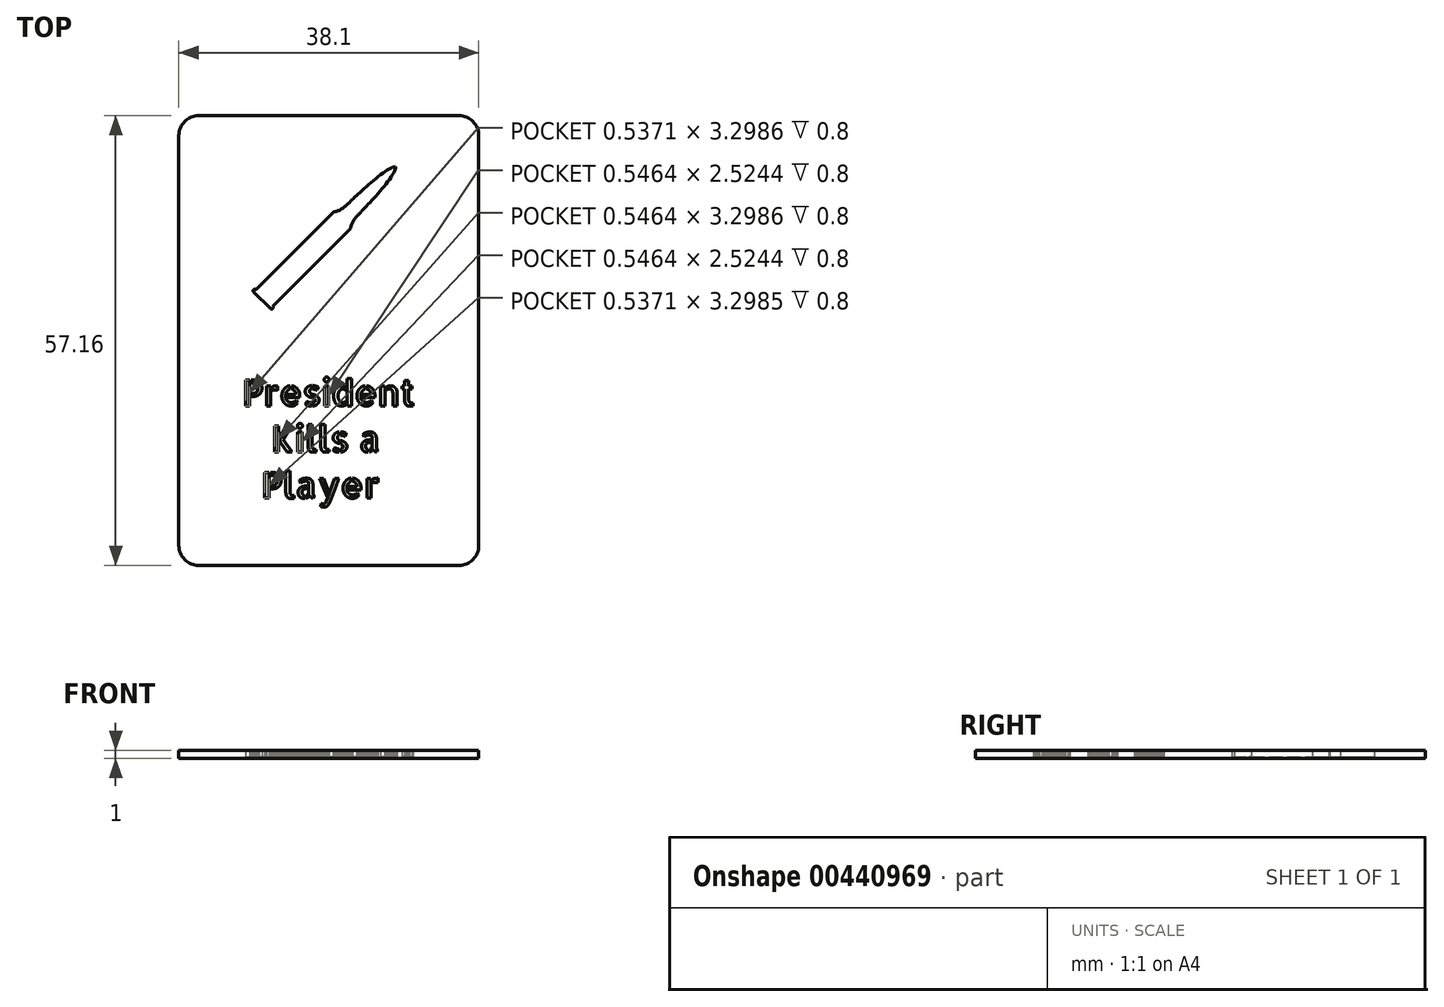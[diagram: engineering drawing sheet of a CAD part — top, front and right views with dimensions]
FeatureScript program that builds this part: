
annotation { "Feature Type Name" : "Feature", "Feature Type Description" : "" }
export const myFeature = defineFeature(function(context is Context, id is Id, definition is map)
    precondition{}
    {
        {
            var Q0;
            Q0=qCreatedBy(makeId("Top.planeOp"),FACE);
            var sketch = newSketch(context, id + "F0", { "sketchPlane" : qUnion([Q0])});
            skLineSegment(sketch, "E0.bottom", {"start": v(16.5, 28.58) * mm, "end": v(-16.51, 28.58) * mm});
            skLineSegment(sketch, "E0.top", {"start": v(16.51, -28.58) * mm, "end": v(-16.5, -28.58) * mm});
            skLineSegment(sketch, "E0.left", {"start": v(19.05, 26.04) * mm, "end": v(19.05, -26.04) * mm});
            skLineSegment(sketch, "E0.right", {"start": v(-19.05, 26.04) * mm, "end": v(-19.05, -26.04) * mm});
            skPoint(sketch, "E1.visualSharp", {"position": v(-19.05, 28.58) * mm});
            skArc(sketch, "E1.filletArc", {"start": v(-16.51, 28.58) * mm, "mid": v(-18.3, 27.83) * mm, "end": v(-19.05, 26.04) * mm});
            skPoint(sketch, "E2.visualSharp", {"position": v(19.05, 28.58) * mm});
            skArc(sketch, "E2.filletArc", {"start": v(19.05, 26.04) * mm, "mid": v(18.3, 27.83) * mm, "end": v(16.5, 28.58) * mm});
            skPoint(sketch, "E3.visualSharp", {"position": v(19.05, -28.58) * mm});
            skArc(sketch, "E3.filletArc", {"start": v(16.51, -28.58) * mm, "mid": v(18.3, -27.83) * mm, "end": v(19.05, -26.04) * mm});
            skPoint(sketch, "E4.visualSharp", {"position": v(-19.05, -28.58) * mm});
            skArc(sketch, "E4.filletArc", {"start": v(-19.05, -26.04) * mm, "mid": v(-18.3, -27.83) * mm, "end": v(-16.5, -28.58) * mm});
            skLineSegment(sketch, "E5", {"start": v(0, 28.58) * mm, "end": v(0, 0) * mm, "construction": true});
            skLineSegment(sketch, "E6", {"start": v(0, 0) * mm, "end": v(0, -28.58) * mm, "construction": true});
            skLineSegment(sketch, "E7", {"start": v(-8.49, 5.1) * mm, "end": v(-7.42, 4.05) * mm});
            skArc(sketch, "E8", {"start": v(-7.42, 4.05) * mm, "mid": v(-7.14, 4.05) * mm, "end": v(-7.14, 4.33) * mm});
            skLineSegment(sketch, "E9", {"start": v(-8.49, 5.1) * mm, "end": v(8.49, 22.08) * mm, "construction": true});
            skLineSegment(sketch, "E10", {"start": v(-7.14, 4.33) * mm, "end": v(2.76, 14.23) * mm});
            skFitSpline(sketch, "E11", {"points": [v(2.76, 14.23) * mm, v(4.17, 16.43) * mm], "startDerivative": vector(0.24, 3.05) * mm, "endDerivative": vector(0.39, 0.48) * mm});
            skFitSpline(sketch, "E12", {"points": [v(4.17, 16.43) * mm, v(8.49, 22.08) * mm], "startDerivative": vector(2.3, 2.45) * mm, "endDerivative": vector(-0.08, 3.52) * mm});
            skFitSpline(sketch, "E13.MirrorCS", {"points": [v(2.84, 17.77) * mm, v(8.49, 22.08) * mm], "startDerivative": vector(2.45, 2.3) * mm, "endDerivative": vector(3.52, -0.08) * mm});
            skFitSpline(sketch, "E14.MirrorCS", {"points": [v(0.64, 16.35) * mm, v(2.84, 17.77) * mm], "startDerivative": vector(3.05, 0.24) * mm, "endDerivative": vector(0.48, 0.39) * mm});
            skLineSegment(sketch, "E15.MirrorCS", {"start": v(-9.26, 6.45) * mm, "end": v(0.64, 16.35) * mm});
            skArc(sketch, "E16.MirrorCS", {"start": v(-9.55, 6.17) * mm, "mid": v(-9.55, 6.45) * mm, "end": v(-9.26, 6.45) * mm});
            skLineSegment(sketch, "E17.MirrorCS", {"start": v(-8.49, 5.1) * mm, "end": v(-9.55, 6.17) * mm});
            skLineSegment(sketch, "E18", {"start": v(0, 13.6) * mm, "end": v(1.06, 12.53) * mm, "construction": true});
            skText(sketch, "E19", { "text": "President\n   Kills a\n  Player", "fontName": "AllertaStencil-Regular.ttf"});
            const initialGuessF0  = {"E19": [-0.011, -0.0083, 1, 0, 0.0033]};
            skSetInitialGuess(sketch, initialGuessF0);
            skSolve(sketch);
        }
        {
            var Q0;
            Q0=qSketchRegion(id+"F0",true);
            var Q1;
            Q1=makeQuery(id+"F0.imprint","IMPRINT",FACE,{"disambiguationData":[TD([[makeQuery(id+"F0.imprint","IMPRINT",EDGE,{"derivedFrom":sQuery(id+"F0.wireOp",EDGE,"1hngZ8Vo-O2Y1-8GoF-9924-SmxzgvlIe6eu")}),1.0]])]});
            var Q2;
            Q2=makeQuery(id+"F0.imprint","IMPRINT",FACE,{"disambiguationData":[TD([[makeQuery(id+"F0.imprint","IMPRINT",EDGE,{"derivedFrom":sQuery(id+"F0.wireOp",EDGE,"v3mnc92D-8hCO-dKtl-YXU8-LdhrgQy31VMY")}),1.0]])]});
            var Q3;
            Q3=makeQuery(id+"F0.imprint","IMPRINT",FACE,{"disambiguationData":[TD([[makeQuery(id+"F0.imprint","IMPRINT",EDGE,{"derivedFrom":sQuery(id+"F0.wireOp",EDGE,"XZppkLhH-C5au-Wygf-dwhr-iVVlCesrx2pO")}),1.0]])]});
            var Q4;
            Q4=makeQuery(id+"F0.imprint","IMPRINT",FACE,{"disambiguationData":[TD([[makeQuery(id+"F0.imprint","IMPRINT",EDGE,{"derivedFrom":sQuery(id+"F0.wireOp",EDGE,"y07g3fre-KKaQ-oYPB-yLvA-0BrsEIY3R70T")}),1.0]])]});
            var Q5;
            Q5=makeQuery(id+"F0.imprint","IMPRINT",FACE,{"disambiguationData":[TD([[makeQuery(id+"F0.imprint","IMPRINT",EDGE,{"derivedFrom":sQuery(id+"F0.wireOp",EDGE,"11e286c5-9b9c-43ac-b103-53d864957ac1.sketch_text.stroke-0")}),-1.0]])]});
            var Q6;
            Q6=makeQuery(id+"F0.imprint","IMPRINT",FACE,{"disambiguationData":[TD([[makeQuery(id+"F0.imprint","IMPRINT",EDGE,{"derivedFrom":sQuery(id+"F0.wireOp",EDGE,"11e286c5-9b9c-43ac-b103-53d864957ac1.sketch_text.stroke-8")}),-1.0]])]});
            var Q7;
            Q7=makeQuery(id+"F0.imprint","IMPRINT",FACE,{"disambiguationData":[TD([[makeQuery(id+"F0.imprint","IMPRINT",EDGE,{"derivedFrom":sQuery(id+"F0.wireOp",EDGE,"11e286c5-9b9c-43ac-b103-53d864957ac1.sketch_text.stroke-4")}),-1.0]])]});
            var Q8;
            Q8=makeQuery(id+"F0.imprint","IMPRINT",FACE,{"disambiguationData":[TD([[makeQuery(id+"F0.imprint","IMPRINT",EDGE,{"derivedFrom":sQuery(id+"F0.wireOp",EDGE,"11e286c5-9b9c-43ac-b103-53d864957ac1.sketch_text.stroke-31")}),-1.0]])]});
            var Q9;
            Q9=makeQuery(id+"F0.imprint","IMPRINT",FACE,{"disambiguationData":[TD([[makeQuery(id+"F0.imprint","IMPRINT",EDGE,{"derivedFrom":sQuery(id+"F0.wireOp",EDGE,"11e286c5-9b9c-43ac-b103-53d864957ac1.sketch_text.stroke-12")}),-1.0]])]});
            var Q10;
            Q10=makeQuery(id+"F0.imprint","IMPRINT",FACE,{"disambiguationData":[TD([[makeQuery(id+"F0.imprint","IMPRINT",EDGE,{"derivedFrom":sQuery(id+"F0.wireOp",EDGE,"11e286c5-9b9c-43ac-b103-53d864957ac1.sketch_text.stroke-96")}),-1.0]])]});
            var Q11;
            Q11=makeQuery(id+"F0.imprint","IMPRINT",FACE,{"disambiguationData":[TD([[makeQuery(id+"F0.imprint","IMPRINT",EDGE,{"derivedFrom":sQuery(id+"F0.wireOp",EDGE,"11e286c5-9b9c-43ac-b103-53d864957ac1.sketch_text.stroke-87")}),-1.0]])]});
            var Q12;
            Q12=makeQuery(id+"F0.imprint","IMPRINT",FACE,{"disambiguationData":[TD([[makeQuery(id+"F0.imprint","IMPRINT",EDGE,{"derivedFrom":sQuery(id+"F0.wireOp",EDGE,"11e286c5-9b9c-43ac-b103-53d864957ac1.sketch_text.stroke-67")}),-1.0]])]});
            var Q13;
            Q13=makeQuery(id+"F0.imprint","IMPRINT",FACE,{"disambiguationData":[TD([[makeQuery(id+"F0.imprint","IMPRINT",EDGE,{"derivedFrom":sQuery(id+"F0.wireOp",EDGE,"11e286c5-9b9c-43ac-b103-53d864957ac1.sketch_text.stroke-81")}),-1.0]])]});
            var Q14;
            Q14=makeQuery(id+"F0.imprint","IMPRINT",FACE,{"disambiguationData":[TD([[makeQuery(id+"F0.imprint","IMPRINT",EDGE,{"derivedFrom":sQuery(id+"F0.wireOp",EDGE,"11e286c5-9b9c-43ac-b103-53d864957ac1.sketch_text.stroke-116")}),-1.0]])]});
            var Q15;
            Q15=makeQuery(id+"F0.imprint","IMPRINT",FACE,{"disambiguationData":[TD([[makeQuery(id+"F0.imprint","IMPRINT",EDGE,{"derivedFrom":sQuery(id+"F0.wireOp",EDGE,"11e286c5-9b9c-43ac-b103-53d864957ac1.sketch_text.stroke-122")}),-1.0]])]});
            var Q16;
            Q16=makeQuery(id+"F0.imprint","IMPRINT",FACE,{"disambiguationData":[TD([[makeQuery(id+"F0.imprint","IMPRINT",EDGE,{"derivedFrom":sQuery(id+"F0.wireOp",EDGE,"11e286c5-9b9c-43ac-b103-53d864957ac1.sketch_text.stroke-110")}),-1.0]])]});
            var Q17;
            Q17=makeQuery(id+"F0.imprint","IMPRINT",FACE,{"disambiguationData":[TD([[makeQuery(id+"F0.imprint","IMPRINT",EDGE,{"derivedFrom":sQuery(id+"F0.wireOp",EDGE,"11e286c5-9b9c-43ac-b103-53d864957ac1.sketch_text.stroke-142")}),-1.0]])]});
            var Q18;
            Q18=makeQuery(id+"F0.imprint","IMPRINT",FACE,{"disambiguationData":[TD([[makeQuery(id+"F0.imprint","IMPRINT",EDGE,{"derivedFrom":sQuery(id+"F0.wireOp",EDGE,"11e286c5-9b9c-43ac-b103-53d864957ac1.sketch_text.stroke-138")}),-1.0]])]});
            var Q19;
            Q19=makeQuery(id+"F0.imprint","IMPRINT",FACE,{"disambiguationData":[TD([[makeQuery(id+"F0.imprint","IMPRINT",EDGE,{"derivedFrom":sQuery(id+"F0.wireOp",EDGE,"11e286c5-9b9c-43ac-b103-53d864957ac1.sketch_text.stroke-170")}),-1.0]])]});
            var Q20;
            Q20=makeQuery(id+"F0.imprint","IMPRINT",FACE,{"disambiguationData":[TD([[makeQuery(id+"F0.imprint","IMPRINT",EDGE,{"derivedFrom":sQuery(id+"F0.wireOp",EDGE,"11e286c5-9b9c-43ac-b103-53d864957ac1.sketch_text.stroke-179")}),-1.0]])]});
            var Q21;
            Q21=makeQuery(id+"F0.imprint","IMPRINT",FACE,{"disambiguationData":[TD([[makeQuery(id+"F0.imprint","IMPRINT",EDGE,{"derivedFrom":sQuery(id+"F0.wireOp",EDGE,"11e286c5-9b9c-43ac-b103-53d864957ac1.sketch_text.stroke-150")}),-1.0]])]});
            var Q22;
            Q22=makeQuery(id+"F0.imprint","IMPRINT",FACE,{"disambiguationData":[TD([[makeQuery(id+"F0.imprint","IMPRINT",EDGE,{"derivedFrom":sQuery(id+"F0.wireOp",EDGE,"11e286c5-9b9c-43ac-b103-53d864957ac1.sketch_text.stroke-164")}),-1.0]])]});
            var Q23;
            Q23=makeQuery(id+"F0.imprint","IMPRINT",FACE,{"disambiguationData":[TD([[makeQuery(id+"F0.imprint","IMPRINT",EDGE,{"derivedFrom":sQuery(id+"F0.wireOp",EDGE,"11e286c5-9b9c-43ac-b103-53d864957ac1.sketch_text.stroke-193")}),-1.0]])]});
            var Q24;
            Q24=makeQuery(id+"F0.imprint","IMPRINT",FACE,{"disambiguationData":[TD([[makeQuery(id+"F0.imprint","IMPRINT",EDGE,{"derivedFrom":sQuery(id+"F0.wireOp",EDGE,"3hOEF64v-dSEU-imgf-cV2M-oAy4Y8LvNKR4")}),1.0]])]});
            var Q25;
            Q25=makeQuery(id+"F0.imprint","IMPRINT",FACE,{"disambiguationData":[TD([[makeQuery(id+"F0.imprint","IMPRINT",EDGE,{"derivedFrom":sQuery(id+"F0.wireOp",EDGE,"d61e87b4-afbc-4eba-b1e1-6c312846f633.1.0.0")}),1.0]])]});
            var Q26;
            Q26=makeQuery(id+"F0.imprint","IMPRINT",FACE,{"disambiguationData":[TD([[makeQuery(id+"F0.imprint","IMPRINT",EDGE,{"derivedFrom":sQuery(id+"F0.wireOp",EDGE,"d61e87b4-afbc-4eba-b1e1-6c312846f633.2.0.0")}),1.0]])]});
            var Q27;
            Q27=makeQuery(id+"F0.imprint","IMPRINT",FACE,{"disambiguationData":[TD([[makeQuery(id+"F0.imprint","IMPRINT",EDGE,{"derivedFrom":sQuery(id+"F0.wireOp",EDGE,"d61e87b4-afbc-4eba-b1e1-6c312846f633.3.0.0")}),1.0]])]});
            var Q28;
            Q28=makeQuery(id+"F0.imprint","IMPRINT",FACE,{"disambiguationData":[TD([[makeQuery(id+"F0.imprint","IMPRINT",EDGE,{"derivedFrom":sQuery(id+"F0.wireOp",EDGE,"d61e87b4-afbc-4eba-b1e1-6c312846f633.4.0.0")}),1.0]])]});
            var Q29;
            Q29=makeQuery(id+"F0.imprint","IMPRINT",FACE,{"disambiguationData":[TD([[makeQuery(id+"F0.imprint","IMPRINT",EDGE,{"derivedFrom":sQuery(id+"F0.wireOp",EDGE,"d61e87b4-afbc-4eba-b1e1-6c312846f633.5.0.0")}),1.0]])]});
            var Q30;
            Q30=makeQuery(id+"F0.imprint","IMPRINT",FACE,{"disambiguationData":[TD([[makeQuery(id+"F0.imprint","IMPRINT",EDGE,{"derivedFrom":sQuery(id+"F0.wireOp",EDGE,"d61e87b4-afbc-4eba-b1e1-6c312846f633.6.0.0")}),1.0]])]});
            var Q31;
            Q31=makeQuery(id+"F0.imprint","IMPRINT",FACE,{"disambiguationData":[TD([[makeQuery(id+"F0.imprint","IMPRINT",EDGE,{"derivedFrom":sQuery(id+"F0.wireOp",EDGE,"d61e87b4-afbc-4eba-b1e1-6c312846f633.7.0.0")}),1.0]])]});
            var Q32;
            Q32=makeQuery(id+"F0.imprint","IMPRINT",FACE,{"disambiguationData":[TD([[makeQuery(id+"F0.imprint","IMPRINT",EDGE,{"derivedFrom":sQuery(id+"F0.wireOp",EDGE,"d61e87b4-afbc-4eba-b1e1-6c312846f633.8.0.0")}),1.0]])]});
            var Q33;
            Q33=makeQuery(id+"F0.imprint","IMPRINT",FACE,{"disambiguationData":[TD([[makeQuery(id+"F0.imprint","IMPRINT",EDGE,{"derivedFrom":sQuery(id+"F0.wireOp",EDGE,"d61e87b4-afbc-4eba-b1e1-6c312846f633.9.0.0")}),1.0]])]});
            var Q34;
            Q34=makeQuery(id+"F0.imprint","IMPRINT",FACE,{"disambiguationData":[TD([[makeQuery(id+"F0.imprint","IMPRINT",EDGE,{"derivedFrom":sQuery(id+"F0.wireOp",EDGE,"d61e87b4-afbc-4eba-b1e1-6c312846f633.10.0.0")}),1.0]])]});
            var Q35;
            Q35=makeQuery(id+"F0.imprint","IMPRINT",FACE,{"disambiguationData":[TD([[makeQuery(id+"F0.imprint","IMPRINT",EDGE,{"derivedFrom":sQuery(id+"F0.wireOp",EDGE,"d61e87b4-afbc-4eba-b1e1-6c312846f633.11.0.0")}),1.0]])]});
            var Q36;
            Q36=makeQuery(id+"F0.imprint","IMPRINT",FACE,{"disambiguationData":[TD([[makeQuery(id+"F0.imprint","IMPRINT",EDGE,{"derivedFrom":sQuery(id+"F0.wireOp",EDGE,"d61e87b4-afbc-4eba-b1e1-6c312846f633.12.0.0")}),1.0]])]});
            var Q37;
            Q37=makeQuery(id+"F0.imprint","IMPRINT",FACE,{"disambiguationData":[TD([[makeQuery(id+"F0.imprint","IMPRINT",EDGE,{"derivedFrom":sQuery(id+"F0.wireOp",EDGE,"d61e87b4-afbc-4eba-b1e1-6c312846f633.13.0.0")}),1.0]])]});
            var Q38;
            Q38=makeQuery(id+"F0.imprint","IMPRINT",FACE,{"disambiguationData":[TD([[makeQuery(id+"F0.imprint","IMPRINT",EDGE,{"derivedFrom":sQuery(id+"F0.wireOp",EDGE,"d61e87b4-afbc-4eba-b1e1-6c312846f633.14.0.0")}),1.0]])]});
            var Q39;
            Q39=makeQuery(id+"F0.imprint","IMPRINT",FACE,{"disambiguationData":[TD([[makeQuery(id+"F0.imprint","IMPRINT",EDGE,{"derivedFrom":sQuery(id+"F0.wireOp",EDGE,"d61e87b4-afbc-4eba-b1e1-6c312846f633.15.0.0")}),1.0]])]});
            var Q40;
            Q40=makeQuery(id+"F0.imprint","IMPRINT",FACE,{"disambiguationData":[TD([[makeQuery(id+"F0.imprint","IMPRINT",EDGE,{"derivedFrom":sQuery(id+"F0.wireOp",EDGE,"d61e87b4-afbc-4eba-b1e1-6c312846f633.16.0.0")}),1.0]])]});
            var Q41;
            Q41=makeQuery(id+"F0.imprint","IMPRINT",FACE,{"disambiguationData":[TD([[makeQuery(id+"F0.imprint","IMPRINT",EDGE,{"derivedFrom":sQuery(id+"F0.wireOp",EDGE,"d61e87b4-afbc-4eba-b1e1-6c312846f633.17.0.0")}),1.0]])]});
            var Q42;
            Q42=makeQuery(id+"F0.imprint","IMPRINT",FACE,{"disambiguationData":[TD([[makeQuery(id+"F0.imprint","IMPRINT",EDGE,{"derivedFrom":sQuery(id+"F0.wireOp",EDGE,"d61e87b4-afbc-4eba-b1e1-6c312846f633.18.0.0")}),1.0]])]});
            var Q43;
            Q43=makeQuery(id+"F0.imprint","IMPRINT",FACE,{"disambiguationData":[TD([[makeQuery(id+"F0.imprint","IMPRINT",EDGE,{"derivedFrom":sQuery(id+"F0.wireOp",EDGE,"d61e87b4-afbc-4eba-b1e1-6c312846f633.19.0.0")}),1.0]])]});
            var Q44;
            Q44=makeQuery(id+"F0.imprint","IMPRINT",FACE,{"disambiguationData":[TD([[makeQuery(id+"F0.imprint","IMPRINT",EDGE,{"derivedFrom":sQuery(id+"F0.wireOp",EDGE,"d61e87b4-afbc-4eba-b1e1-6c312846f633.20.0.0")}),1.0]])]});
            var Q45;
            Q45=makeQuery(id+"F0.imprint","IMPRINT",FACE,{"disambiguationData":[TD([[makeQuery(id+"F0.imprint","IMPRINT",EDGE,{"derivedFrom":sQuery(id+"F0.wireOp",EDGE,"d61e87b4-afbc-4eba-b1e1-6c312846f633.21.0.0")}),1.0]])]});
            var Q46;
            Q46=makeQuery(id+"F0.imprint","IMPRINT",FACE,{"disambiguationData":[TD([[makeQuery(id+"F0.imprint","IMPRINT",EDGE,{"derivedFrom":sQuery(id+"F0.wireOp",EDGE,"824da2b7-0e67-4436-b530-e222e440d070.sketch_text.stroke-0")}),-1.0]])]});
            var Q47;
            Q47=makeQuery(id+"F0.imprint","IMPRINT",FACE,{"disambiguationData":[TD([[makeQuery(id+"F0.imprint","IMPRINT",EDGE,{"derivedFrom":sQuery(id+"F0.wireOp",EDGE,"824da2b7-0e67-4436-b530-e222e440d070.sketch_text.stroke-15")}),-1.0]])]});
            var Q48;
            Q48=makeQuery(id+"F0.imprint","IMPRINT",FACE,{"disambiguationData":[TD([[makeQuery(id+"F0.imprint","IMPRINT",EDGE,{"derivedFrom":sQuery(id+"F0.wireOp",EDGE,"824da2b7-0e67-4436-b530-e222e440d070.sketch_text.stroke-32")}),-1.0]])]});
            var Q49;
            Q49=makeQuery(id+"F0.imprint","IMPRINT",FACE,{"disambiguationData":[TD([[makeQuery(id+"F0.imprint","IMPRINT",EDGE,{"derivedFrom":sQuery(id+"F0.wireOp",EDGE,"824da2b7-0e67-4436-b530-e222e440d070.sketch_text.stroke-54")}),-1.0]])]});
            var Q50;
            Q50=makeQuery(id+"F0.imprint","IMPRINT",FACE,{"disambiguationData":[TD([[makeQuery(id+"F0.imprint","IMPRINT",EDGE,{"derivedFrom":sQuery(id+"F0.wireOp",EDGE,"824da2b7-0e67-4436-b530-e222e440d070.sketch_text.stroke-50")}),-1.0]])]});
            var Q51;
            Q51=makeQuery(id+"F0.imprint","IMPRINT",FACE,{"disambiguationData":[TD([[makeQuery(id+"F0.imprint","IMPRINT",EDGE,{"derivedFrom":sQuery(id+"F0.wireOp",EDGE,"824da2b7-0e67-4436-b530-e222e440d070.sketch_text.stroke-58")}),-1.0]])]});
            var Q52;
            Q52=makeQuery(id+"F0.imprint","IMPRINT",FACE,{"disambiguationData":[TD([[makeQuery(id+"F0.imprint","IMPRINT",EDGE,{"derivedFrom":sQuery(id+"F0.wireOp",EDGE,"824da2b7-0e67-4436-b530-e222e440d070.sketch_text.stroke-75")}),-1.0]])]});
            var Q53;
            Q53=makeQuery(id+"F0.imprint","IMPRINT",FACE,{"disambiguationData":[TD([[makeQuery(id+"F0.imprint","IMPRINT",EDGE,{"derivedFrom":sQuery(id+"F0.wireOp",EDGE,"824da2b7-0e67-4436-b530-e222e440d070.sketch_text.stroke-79")}),-1.0]])]});
            var Q54;
            Q54=makeQuery(id+"F0.imprint","IMPRINT",FACE,{"disambiguationData":[TD([[makeQuery(id+"F0.imprint","IMPRINT",EDGE,{"derivedFrom":sQuery(id+"F0.wireOp",EDGE,"prHT7NwA-CJht-v5NG-W2o7-Xqmxs18joHLs.bottom")}),-1.0]])]});
            var Q55;
            Q55=makeQuery(id+"F0.imprint","IMPRINT",FACE,{"disambiguationData":[TD([[makeQuery(id+"F0.imprint","IMPRINT",EDGE,{"derivedFrom":sQuery(id+"F0.wireOp",EDGE,"loqv97KZ-vKno-A8WI-mPE9-OnQyIJFUs6ra.bottom")}),-1.0]])]});
            var Q56;
            Q56=makeQuery(id+"F0.imprint","IMPRINT",FACE,{"disambiguationData":[TD([[makeQuery(id+"F0.imprint","IMPRINT",EDGE,{"derivedFrom":sQuery(id+"F0.wireOp",EDGE,"IiW4FtL9-cIlY-GVfC-fHN8-Muj6rfwzQ4Nk.bottom")}),-1.0]])]});
            var Q57;
            Q57=makeQuery(id+"F0.imprint","IMPRINT",FACE,{"disambiguationData":[TD([[makeQuery(id+"F0.imprint","IMPRINT",EDGE,{"derivedFrom":sQuery(id+"F0.wireOp",EDGE,"hgyYalZY-fuKV-cGhY-Ue2A-NU4bW9GvdhIw.bottom")}),-1.0]])]});
            var Q58;
            Q58=makeQuery(id+"F0.imprint","IMPRINT",FACE,{"disambiguationData":[TD([[makeQuery(id+"F0.imprint","IMPRINT",EDGE,{"derivedFrom":sQuery(id+"F0.wireOp",EDGE,"7RaPNTs9-LwY4-UvGH-fbjw-P0gIc8EvOOef.bottom")}),-1.0]])]});
            var Q59;
            Q59=makeQuery(id+"F0.imprint","IMPRINT",FACE,{"disambiguationData":[TD([[makeQuery(id+"F0.imprint","IMPRINT",EDGE,{"derivedFrom":sQuery(id+"F0.wireOp",EDGE,"0Oy3iZBW-l60p-ye98-HsD0-8aETsZGMw3y6.bottom")}),-1.0]])]});
            var Q60;
            Q60=makeQuery(id+"F0.imprint","IMPRINT",FACE,{"disambiguationData":[TD([[makeQuery(id+"F0.imprint","IMPRINT",EDGE,{"derivedFrom":sQuery(id+"F0.wireOp",EDGE,"uO9PoV1c-vtol-dT46-PGAY-6wPjbnXBpNAn.bottom")}),-1.0]])]});
            var Q61;
            Q61=makeQuery(id+"F0.imprint","IMPRINT",FACE,{"disambiguationData":[TD([[makeQuery(id+"F0.imprint","IMPRINT",EDGE,{"derivedFrom":sQuery(id+"F0.wireOp",EDGE,"HzYubSo2-mYeH-qRyi-21AG-W6rulPkjMyM9.bottom")}),-1.0]])]});
            extrude(context, id + "F1", {"entities" : qUnion([Q0, Q1, Q2, Q3, Q4, Q5, Q6, Q7, Q8, Q9, Q10, Q11, Q12, Q13, Q14, Q15, Q16, Q17, Q18, Q19, Q20, Q21, Q22, Q23, Q24, Q25, Q26, Q27, Q28, Q29, Q30, Q31, Q32, Q33, Q34, Q35, Q36, Q37, Q38, Q39, Q40, Q41, Q42, Q43, Q44, Q45, Q46, Q47, Q48, Q49, Q50, Q51, Q52, Q53, Q54, Q55, Q56, Q57, Q58, Q59, Q60, Q61]), "depth" : 1 * mm});
        }
        {
            var Q0;
            Q0=makeQuery(id+"F0.imprint","IMPRINT",FACE,{"disambiguationData":[TD([[makeQuery(id+"F0.imprint","IMPRINT",EDGE,{"derivedFrom":sQuery(id+"F0.wireOp",EDGE,"E7")}),1.0]])]});
            var Q1;
            Q1=makeQuery(id+"F0.imprint","IMPRINT",FACE,{"disambiguationData":[TD([[makeQuery(id+"F0.imprint","IMPRINT",EDGE,{"derivedFrom":sQuery(id+"F0.wireOp",EDGE,"E19.sketch_text.stroke-77")}),-1.0]])]});
            var Q2;
            Q2=makeQuery(id+"F0.imprint","IMPRINT",FACE,{"disambiguationData":[TD([[makeQuery(id+"F0.imprint","IMPRINT",EDGE,{"derivedFrom":sQuery(id+"F0.wireOp",EDGE,"E19.sketch_text.stroke-533")}),-1.0]])]});
            var Q3;
            Q3=makeQuery(id+"F0.imprint","IMPRINT",FACE,{"disambiguationData":[TD([[makeQuery(id+"F0.imprint","IMPRINT",EDGE,{"derivedFrom":sQuery(id+"F0.wireOp",EDGE,"E19.sketch_text.stroke-162")}),-1.0]])]});
            var Q4;
            Q4=makeQuery(id+"F0.imprint","IMPRINT",FACE,{"disambiguationData":[TD([[makeQuery(id+"F0.imprint","IMPRINT",EDGE,{"derivedFrom":sQuery(id+"F0.wireOp",EDGE,"E19.sketch_text.stroke-175")}),-1.0]])]});
            var Q5;
            Q5=makeQuery(id+"F0.imprint","IMPRINT",FACE,{"disambiguationData":[TD([[makeQuery(id+"F0.imprint","IMPRINT",EDGE,{"derivedFrom":sQuery(id+"F0.wireOp",EDGE,"E19.sketch_text.stroke-468")}),-1.0]])]});
            var Q6;
            Q6=makeQuery(id+"F0.imprint","IMPRINT",FACE,{"disambiguationData":[TD([[makeQuery(id+"F0.imprint","IMPRINT",EDGE,{"derivedFrom":sQuery(id+"F0.wireOp",EDGE,"E19.sketch_text.stroke-132")}),-1.0]])]});
            var Q7;
            Q7=makeQuery(id+"F0.imprint","IMPRINT",FACE,{"disambiguationData":[TD([[makeQuery(id+"F0.imprint","IMPRINT",EDGE,{"derivedFrom":sQuery(id+"F0.wireOp",EDGE,"E19.sketch_text.stroke-97")}),-1.0]])]});
            var Q8;
            Q8=makeQuery(id+"F0.imprint","IMPRINT",FACE,{"disambiguationData":[TD([[makeQuery(id+"F0.imprint","IMPRINT",EDGE,{"derivedFrom":sQuery(id+"F0.wireOp",EDGE,"E19.sketch_text.stroke-577")}),-1.0]])]});
            var Q9;
            Q9=makeQuery(id+"F0.imprint","IMPRINT",FACE,{"disambiguationData":[TD([[makeQuery(id+"F0.imprint","IMPRINT",EDGE,{"derivedFrom":sQuery(id+"F0.wireOp",EDGE,"E19.sketch_text.stroke-570")}),-1.0]])]});
            var Q10;
            Q10=makeQuery(id+"F0.imprint","IMPRINT",FACE,{"disambiguationData":[TD([[makeQuery(id+"F0.imprint","IMPRINT",EDGE,{"derivedFrom":sQuery(id+"F0.wireOp",EDGE,"E19.sketch_text.stroke-307")}),-1.0]])]});
            var Q11;
            Q11=makeQuery(id+"F0.imprint","IMPRINT",FACE,{"disambiguationData":[TD([[makeQuery(id+"F0.imprint","IMPRINT",EDGE,{"derivedFrom":sQuery(id+"F0.wireOp",EDGE,"E19.sketch_text.stroke-252")}),-1.0]])]});
            var Q12;
            Q12=makeQuery(id+"F0.imprint","IMPRINT",FACE,{"disambiguationData":[TD([[makeQuery(id+"F0.imprint","IMPRINT",EDGE,{"derivedFrom":sQuery(id+"F0.wireOp",EDGE,"E19.sketch_text.stroke-528")}),-1.0]])]});
            var Q13;
            Q13=makeQuery(id+"F0.imprint","IMPRINT",FACE,{"disambiguationData":[TD([[makeQuery(id+"F0.imprint","IMPRINT",EDGE,{"derivedFrom":sQuery(id+"F0.wireOp",EDGE,"E19.sketch_text.stroke-53")}),-1.0]])]});
            var Q14;
            Q14=makeQuery(id+"F0.imprint","IMPRINT",FACE,{"disambiguationData":[TD([[makeQuery(id+"F0.imprint","IMPRINT",EDGE,{"derivedFrom":sQuery(id+"F0.wireOp",EDGE,"E19.sketch_text.stroke-271")}),-1.0]])]});
            var Q15;
            Q15=makeQuery(id+"F0.imprint","IMPRINT",FACE,{"disambiguationData":[TD([[makeQuery(id+"F0.imprint","IMPRINT",EDGE,{"derivedFrom":sQuery(id+"F0.wireOp",EDGE,"E19.sketch_text.stroke-409")}),-1.0]])]});
            var Q16;
            Q16=makeQuery(id+"F0.imprint","IMPRINT",FACE,{"disambiguationData":[TD([[makeQuery(id+"F0.imprint","IMPRINT",EDGE,{"derivedFrom":sQuery(id+"F0.wireOp",EDGE,"E19.sketch_text.stroke-199")}),-1.0]])]});
            var Q17;
            Q17=makeQuery(id+"F0.imprint","IMPRINT",FACE,{"disambiguationData":[TD([[makeQuery(id+"F0.imprint","IMPRINT",EDGE,{"derivedFrom":sQuery(id+"F0.wireOp",EDGE,"E19.sketch_text.stroke-431")}),-1.0]])]});
            var Q18;
            Q18=makeQuery(id+"F0.imprint","IMPRINT",FACE,{"disambiguationData":[TD([[makeQuery(id+"F0.imprint","IMPRINT",EDGE,{"derivedFrom":sQuery(id+"F0.wireOp",EDGE,"E19.sketch_text.stroke-289")}),-1.0]])]});
            var Q19;
            Q19=makeQuery(id+"F0.imprint","IMPRINT",FACE,{"disambiguationData":[TD([[makeQuery(id+"F0.imprint","IMPRINT",EDGE,{"derivedFrom":sQuery(id+"F0.wireOp",EDGE,"E19.sketch_text.stroke-4")}),-1.0]])]});
            var Q20;
            Q20=makeQuery(id+"F0.imprint","IMPRINT",FACE,{"disambiguationData":[TD([[makeQuery(id+"F0.imprint","IMPRINT",EDGE,{"derivedFrom":sQuery(id+"F0.wireOp",EDGE,"E19.sketch_text.stroke-546")}),-1.0]])]});
            var Q21;
            Q21=makeQuery(id+"F0.imprint","IMPRINT",FACE,{"disambiguationData":[TD([[makeQuery(id+"F0.imprint","IMPRINT",EDGE,{"derivedFrom":sQuery(id+"F0.wireOp",EDGE,"E19.sketch_text.stroke-223")}),-1.0]])]});
            var Q22;
            Q22=makeQuery(id+"F0.imprint","IMPRINT",FACE,{"disambiguationData":[TD([[makeQuery(id+"F0.imprint","IMPRINT",EDGE,{"derivedFrom":sQuery(id+"F0.wireOp",EDGE,"E19.sketch_text.stroke-204")}),-1.0]])]});
            var Q23;
            Q23=makeQuery(id+"F0.imprint","IMPRINT",FACE,{"disambiguationData":[TD([[makeQuery(id+"F0.imprint","IMPRINT",EDGE,{"derivedFrom":sQuery(id+"F0.wireOp",EDGE,"E19.sketch_text.stroke-137")}),-1.0]])]});
            var Q24;
            Q24=makeQuery(id+"F0.imprint","IMPRINT",FACE,{"disambiguationData":[TD([[makeQuery(id+"F0.imprint","IMPRINT",EDGE,{"derivedFrom":sQuery(id+"F0.wireOp",EDGE,"E19.sketch_text.stroke-504")}),-1.0]])]});
            var Q25;
            Q25=makeQuery(id+"F0.imprint","IMPRINT",FACE,{"disambiguationData":[TD([[makeQuery(id+"F0.imprint","IMPRINT",EDGE,{"derivedFrom":sQuery(id+"F0.wireOp",EDGE,"E19.sketch_text.stroke-405")}),-1.0]])]});
            var Q26;
            Q26=makeQuery(id+"F0.imprint","IMPRINT",FACE,{"disambiguationData":[TD([[makeQuery(id+"F0.imprint","IMPRINT",EDGE,{"derivedFrom":sQuery(id+"F0.wireOp",EDGE,"E19.sketch_text.stroke-248")}),-1.0]])]});
            var Q27;
            Q27=makeQuery(id+"F0.imprint","IMPRINT",FACE,{"disambiguationData":[TD([[makeQuery(id+"F0.imprint","IMPRINT",EDGE,{"derivedFrom":sQuery(id+"F0.wireOp",EDGE,"E19.sketch_text.stroke-336")}),-1.0]])]});
            var Q28;
            Q28=makeQuery(id+"F0.imprint","IMPRINT",FACE,{"disambiguationData":[TD([[makeQuery(id+"F0.imprint","IMPRINT",EDGE,{"derivedFrom":sQuery(id+"F0.wireOp",EDGE,"E19.sketch_text.stroke-369")}),-1.0]])]});
            var Q29;
            Q29=makeQuery(id+"F0.imprint","IMPRINT",FACE,{"disambiguationData":[TD([[makeQuery(id+"F0.imprint","IMPRINT",EDGE,{"derivedFrom":sQuery(id+"F0.wireOp",EDGE,"E19.sketch_text.stroke-350")}),-1.0]])]});
            var Q30;
            Q30=makeQuery(id+"F0.imprint","IMPRINT",FACE,{"disambiguationData":[TD([[makeQuery(id+"F0.imprint","IMPRINT",EDGE,{"derivedFrom":sQuery(id+"F0.wireOp",EDGE,"E19.sketch_text.stroke-449")}),-1.0]])]});
            var Q31;
            Q31=makeQuery(id+"F0.imprint","IMPRINT",FACE,{"disambiguationData":[TD([[makeQuery(id+"F0.imprint","IMPRINT",EDGE,{"derivedFrom":sQuery(id+"F0.wireOp",EDGE,"E19.sketch_text.stroke-327")}),-1.0]])]});
            var Q32;
            Q32=makeQuery(id+"F0.imprint","IMPRINT",FACE,{"disambiguationData":[TD([[makeQuery(id+"F0.imprint","IMPRINT",EDGE,{"derivedFrom":sQuery(id+"F0.wireOp",EDGE,"E19.sketch_text.stroke-263")}),-1.0]])]});
            var Q33;
            Q33=makeQuery(id+"F0.imprint","IMPRINT",FACE,{"disambiguationData":[TD([[makeQuery(id+"F0.imprint","IMPRINT",EDGE,{"derivedFrom":sQuery(id+"F0.wireOp",EDGE,"E19.sketch_text.stroke-120")}),-1.0]])]});
            var Q34;
            Q34=makeQuery(id+"F0.imprint","IMPRINT",FACE,{"disambiguationData":[TD([[makeQuery(id+"F0.imprint","IMPRINT",EDGE,{"derivedFrom":sQuery(id+"F0.wireOp",EDGE,"E19.sketch_text.stroke-0")}),-1.0]])]});
            var Q35;
            Q35=makeQuery(id+"F0.imprint","IMPRINT",FACE,{"disambiguationData":[TD([[makeQuery(id+"F0.imprint","IMPRINT",EDGE,{"derivedFrom":sQuery(id+"F0.wireOp",EDGE,"E19.sketch_text.stroke-40")}),-1.0]])]});
            var Q36;
            Q36=makeQuery(id+"F0.imprint","IMPRINT",FACE,{"disambiguationData":[TD([[makeQuery(id+"F0.imprint","IMPRINT",EDGE,{"derivedFrom":sQuery(id+"F0.wireOp",EDGE,"E19.sketch_text.stroke-321")}),-1.0]])]});
            var Q37;
            Q37=makeQuery(id+"F0.imprint","IMPRINT",FACE,{"disambiguationData":[TD([[makeQuery(id+"F0.imprint","IMPRINT",EDGE,{"derivedFrom":sQuery(id+"F0.wireOp",EDGE,"E19.sketch_text.stroke-33")}),-1.0]])]});
            var Q38;
            Q38=makeQuery(id+"F0.imprint","IMPRINT",FACE,{"disambiguationData":[TD([[makeQuery(id+"F0.imprint","IMPRINT",EDGE,{"derivedFrom":sQuery(id+"F0.wireOp",EDGE,"E19.sketch_text.stroke-26")}),-1.0]])]});
            var Q39;
            Q39=makeQuery(id+"F0.imprint","IMPRINT",FACE,{"disambiguationData":[TD([[makeQuery(id+"F0.imprint","IMPRINT",EDGE,{"derivedFrom":sQuery(id+"F0.wireOp",EDGE,"E19.sketch_text.stroke-106")}),-1.0]])]});
            var Q40;
            Q40=makeQuery(id+"F0.imprint","IMPRINT",FACE,{"disambiguationData":[TD([[makeQuery(id+"F0.imprint","IMPRINT",EDGE,{"derivedFrom":sQuery(id+"F0.wireOp",EDGE,"E19.sketch_text.stroke-259")}),-1.0]])]});
            var Q41;
            Q41=makeQuery(id+"F0.imprint","IMPRINT",FACE,{"disambiguationData":[TD([[makeQuery(id+"F0.imprint","IMPRINT",EDGE,{"derivedFrom":sQuery(id+"F0.wireOp",EDGE,"E19.sketch_text.stroke-91")}),-1.0]])]});
            var Q42;
            Q42=makeQuery(id+"F0.imprint","IMPRINT",FACE,{"disambiguationData":[TD([[makeQuery(id+"F0.imprint","IMPRINT",EDGE,{"derivedFrom":sQuery(id+"F0.wireOp",EDGE,"E19.sketch_text.stroke-124")}),-1.0]])]});
            extrude(context, id + "F2", {"entities" : qUnion([Q0, Q1, Q2, Q3, Q4, Q5, Q6, Q7, Q8, Q9, Q10, Q11, Q12, Q13, Q14, Q15, Q16, Q17, Q18, Q19, Q20, Q21, Q22, Q23, Q24, Q25, Q26, Q27, Q28, Q29, Q30, Q31, Q32, Q33, Q34, Q35, Q36, Q37, Q38, Q39, Q40, Q41, Q42]), "operationType" : NewBodyOperationType.ADD, "depth" : .2 * mm, "offsetDistance" : 25 * mm});
        }
        {
            var Q0;
            Q0=makeQuery(id+"F0.imprint","IMPRINT",FACE,{"disambiguationData":[TD([[makeQuery(id+"F0.imprint","IMPRINT",EDGE,{"derivedFrom":sQuery(id+"F0.wireOp",EDGE,"E19.sketch_text.stroke-369")}),-1.0]])]});
            var Q1;
            Q1=makeQuery(id+"F0.imprint","IMPRINT",FACE,{"disambiguationData":[TD([[makeQuery(id+"F0.imprint","IMPRINT",EDGE,{"derivedFrom":sQuery(id+"F0.wireOp",EDGE,"E19.sketch_text.stroke-336")}),-1.0]])]});
            var Q2;
            Q2=makeQuery(id+"F0.imprint","IMPRINT",FACE,{"disambiguationData":[TD([[makeQuery(id+"F0.imprint","IMPRINT",EDGE,{"derivedFrom":sQuery(id+"F0.wireOp",EDGE,"E19.sketch_text.stroke-350")}),-1.0]])]});
            var Q3;
            Q3=makeQuery(id+"F0.imprint","IMPRINT",FACE,{"disambiguationData":[TD([[makeQuery(id+"F0.imprint","IMPRINT",EDGE,{"derivedFrom":sQuery(id+"F0.wireOp",EDGE,"E19.sketch_text.stroke-175")}),-1.0]])]});
            var Q4;
            Q4=makeQuery(id+"F0.imprint","IMPRINT",FACE,{"disambiguationData":[TD([[makeQuery(id+"F0.imprint","IMPRINT",EDGE,{"derivedFrom":sQuery(id+"F0.wireOp",EDGE,"E19.sketch_text.stroke-405")}),-1.0]])]});
            var Q5;
            Q5=makeQuery(id+"F0.imprint","IMPRINT",FACE,{"disambiguationData":[TD([[makeQuery(id+"F0.imprint","IMPRINT",EDGE,{"derivedFrom":sQuery(id+"F0.wireOp",EDGE,"E19.sketch_text.stroke-409")}),-1.0]])]});
            var Q6;
            Q6=makeQuery(id+"F0.imprint","IMPRINT",FACE,{"disambiguationData":[TD([[makeQuery(id+"F0.imprint","IMPRINT",EDGE,{"derivedFrom":sQuery(id+"F0.wireOp",EDGE,"E19.sketch_text.stroke-204")}),-1.0]])]});
            var Q7;
            Q7=makeQuery(id+"F0.imprint","IMPRINT",FACE,{"disambiguationData":[TD([[makeQuery(id+"F0.imprint","IMPRINT",EDGE,{"derivedFrom":sQuery(id+"F0.wireOp",EDGE,"E19.sketch_text.stroke-431")}),-1.0]])]});
            var Q8;
            Q8=makeQuery(id+"F0.imprint","IMPRINT",FACE,{"disambiguationData":[TD([[makeQuery(id+"F0.imprint","IMPRINT",EDGE,{"derivedFrom":sQuery(id+"F0.wireOp",EDGE,"E19.sketch_text.stroke-223")}),-1.0]])]});
            var Q9;
            Q9=makeQuery(id+"F0.imprint","IMPRINT",FACE,{"disambiguationData":[TD([[makeQuery(id+"F0.imprint","IMPRINT",EDGE,{"derivedFrom":sQuery(id+"F0.wireOp",EDGE,"E19.sketch_text.stroke-449")}),-1.0]])]});
            var Q10;
            Q10=makeQuery(id+"F0.imprint","IMPRINT",FACE,{"disambiguationData":[TD([[makeQuery(id+"F0.imprint","IMPRINT",EDGE,{"derivedFrom":sQuery(id+"F0.wireOp",EDGE,"E19.sketch_text.stroke-248")}),-1.0]])]});
            var Q11;
            Q11=makeQuery(id+"F0.imprint","IMPRINT",FACE,{"disambiguationData":[TD([[makeQuery(id+"F0.imprint","IMPRINT",EDGE,{"derivedFrom":sQuery(id+"F0.wireOp",EDGE,"E19.sketch_text.stroke-468")}),-1.0]])]});
            var Q12;
            Q12=makeQuery(id+"F0.imprint","IMPRINT",FACE,{"disambiguationData":[TD([[makeQuery(id+"F0.imprint","IMPRINT",EDGE,{"derivedFrom":sQuery(id+"F0.wireOp",EDGE,"E19.sketch_text.stroke-252")}),-1.0]])]});
            var Q13;
            Q13=makeQuery(id+"F0.imprint","IMPRINT",FACE,{"disambiguationData":[TD([[makeQuery(id+"F0.imprint","IMPRINT",EDGE,{"derivedFrom":sQuery(id+"F0.wireOp",EDGE,"E19.sketch_text.stroke-504")}),-1.0]])]});
            var Q14;
            Q14=makeQuery(id+"F0.imprint","IMPRINT",FACE,{"disambiguationData":[TD([[makeQuery(id+"F0.imprint","IMPRINT",EDGE,{"derivedFrom":sQuery(id+"F0.wireOp",EDGE,"E19.sketch_text.stroke-528")}),-1.0]])]});
            var Q15;
            Q15=makeQuery(id+"F0.imprint","IMPRINT",FACE,{"disambiguationData":[TD([[makeQuery(id+"F0.imprint","IMPRINT",EDGE,{"derivedFrom":sQuery(id+"F0.wireOp",EDGE,"E19.sketch_text.stroke-259")}),-1.0]])]});
            var Q16;
            Q16=makeQuery(id+"F0.imprint","IMPRINT",FACE,{"disambiguationData":[TD([[makeQuery(id+"F0.imprint","IMPRINT",EDGE,{"derivedFrom":sQuery(id+"F0.wireOp",EDGE,"E19.sketch_text.stroke-546")}),-1.0]])]});
            var Q17;
            Q17=makeQuery(id+"F0.imprint","IMPRINT",FACE,{"disambiguationData":[TD([[makeQuery(id+"F0.imprint","IMPRINT",EDGE,{"derivedFrom":sQuery(id+"F0.wireOp",EDGE,"E19.sketch_text.stroke-271")}),-1.0]])]});
            var Q18;
            Q18=makeQuery(id+"F0.imprint","IMPRINT",FACE,{"disambiguationData":[TD([[makeQuery(id+"F0.imprint","IMPRINT",EDGE,{"derivedFrom":sQuery(id+"F0.wireOp",EDGE,"E19.sketch_text.stroke-570")}),-1.0]])]});
            var Q19;
            Q19=makeQuery(id+"F0.imprint","IMPRINT",FACE,{"disambiguationData":[TD([[makeQuery(id+"F0.imprint","IMPRINT",EDGE,{"derivedFrom":sQuery(id+"F0.wireOp",EDGE,"E19.sketch_text.stroke-289")}),-1.0]])]});
            var Q20;
            Q20=makeQuery(id+"F0.imprint","IMPRINT",FACE,{"disambiguationData":[TD([[makeQuery(id+"F0.imprint","IMPRINT",EDGE,{"derivedFrom":sQuery(id+"F0.wireOp",EDGE,"E19.sketch_text.stroke-321")}),-1.0]])]});
            var Q21;
            Q21=makeQuery(id+"F0.imprint","IMPRINT",FACE,{"disambiguationData":[TD([[makeQuery(id+"F0.imprint","IMPRINT",EDGE,{"derivedFrom":sQuery(id+"F0.wireOp",EDGE,"E19.sketch_text.stroke-162")}),-1.0]])]});
            var Q22;
            Q22=makeQuery(id+"F0.imprint","IMPRINT",FACE,{"disambiguationData":[TD([[makeQuery(id+"F0.imprint","IMPRINT",EDGE,{"derivedFrom":sQuery(id+"F0.wireOp",EDGE,"E19.sketch_text.stroke-132")}),-1.0]])]});
            var Q23;
            Q23=makeQuery(id+"F0.imprint","IMPRINT",FACE,{"disambiguationData":[TD([[makeQuery(id+"F0.imprint","IMPRINT",EDGE,{"derivedFrom":sQuery(id+"F0.wireOp",EDGE,"E19.sketch_text.stroke-137")}),-1.0]])]});
            var Q24;
            Q24=makeQuery(id+"F0.imprint","IMPRINT",FACE,{"disambiguationData":[TD([[makeQuery(id+"F0.imprint","IMPRINT",EDGE,{"derivedFrom":sQuery(id+"F0.wireOp",EDGE,"E7")}),1.0]])]});
            var Q25;
            Q25=makeQuery(id+"F0.imprint","IMPRINT",FACE,{"disambiguationData":[TD([[makeQuery(id+"F0.imprint","IMPRINT",EDGE,{"derivedFrom":sQuery(id+"F0.wireOp",EDGE,"E19.sketch_text.stroke-0")}),-1.0]])]});
            var Q26;
            Q26=makeQuery(id+"F0.imprint","IMPRINT",FACE,{"disambiguationData":[TD([[makeQuery(id+"F0.imprint","IMPRINT",EDGE,{"derivedFrom":sQuery(id+"F0.wireOp",EDGE,"E19.sketch_text.stroke-4")}),-1.0]])]});
            var Q27;
            Q27=makeQuery(id+"F0.imprint","IMPRINT",FACE,{"disambiguationData":[TD([[makeQuery(id+"F0.imprint","IMPRINT",EDGE,{"derivedFrom":sQuery(id+"F0.wireOp",EDGE,"E19.sketch_text.stroke-26")}),-1.0]])]});
            var Q28;
            Q28=makeQuery(id+"F0.imprint","IMPRINT",FACE,{"disambiguationData":[TD([[makeQuery(id+"F0.imprint","IMPRINT",EDGE,{"derivedFrom":sQuery(id+"F0.wireOp",EDGE,"E19.sketch_text.stroke-33")}),-1.0]])]});
            var Q29;
            Q29=makeQuery(id+"F0.imprint","IMPRINT",FACE,{"disambiguationData":[TD([[makeQuery(id+"F0.imprint","IMPRINT",EDGE,{"derivedFrom":sQuery(id+"F0.wireOp",EDGE,"E19.sketch_text.stroke-40")}),-1.0]])]});
            var Q30;
            Q30=makeQuery(id+"F0.imprint","IMPRINT",FACE,{"disambiguationData":[TD([[makeQuery(id+"F0.imprint","IMPRINT",EDGE,{"derivedFrom":sQuery(id+"F0.wireOp",EDGE,"E19.sketch_text.stroke-53")}),-1.0]])]});
            var Q31;
            Q31=makeQuery(id+"F0.imprint","IMPRINT",FACE,{"disambiguationData":[TD([[makeQuery(id+"F0.imprint","IMPRINT",EDGE,{"derivedFrom":sQuery(id+"F0.wireOp",EDGE,"E19.sketch_text.stroke-77")}),-1.0]])]});
            var Q32;
            Q32=makeQuery(id+"F0.imprint","IMPRINT",FACE,{"disambiguationData":[TD([[makeQuery(id+"F0.imprint","IMPRINT",EDGE,{"derivedFrom":sQuery(id+"F0.wireOp",EDGE,"E19.sketch_text.stroke-106")}),-1.0]])]});
            var Q33;
            Q33=makeQuery(id+"F0.imprint","IMPRINT",FACE,{"disambiguationData":[TD([[makeQuery(id+"F0.imprint","IMPRINT",EDGE,{"derivedFrom":sQuery(id+"F0.wireOp",EDGE,"E19.sketch_text.stroke-120")}),-1.0]])]});
            var Q34;
            Q34=makeQuery(id+"F0.imprint","IMPRINT",FACE,{"disambiguationData":[TD([[makeQuery(id+"F0.imprint","IMPRINT",EDGE,{"derivedFrom":sQuery(id+"F0.wireOp",EDGE,"E19.sketch_text.stroke-199")}),-1.0]])]});
            var Q35;
            Q35=makeQuery(id+"F0.imprint","IMPRINT",FACE,{"disambiguationData":[TD([[makeQuery(id+"F0.imprint","IMPRINT",EDGE,{"derivedFrom":sQuery(id+"F0.wireOp",EDGE,"E19.sketch_text.stroke-533")}),-1.0]])]});
            var Q36;
            Q36=makeQuery(id+"F0.imprint","IMPRINT",FACE,{"disambiguationData":[TD([[makeQuery(id+"F0.imprint","IMPRINT",EDGE,{"derivedFrom":sQuery(id+"F0.wireOp",EDGE,"E19.sketch_text.stroke-263")}),-1.0]])]});
            var Q37;
            Q37=makeQuery(id+"F0.imprint","IMPRINT",FACE,{"disambiguationData":[TD([[makeQuery(id+"F0.imprint","IMPRINT",EDGE,{"derivedFrom":sQuery(id+"F0.wireOp",EDGE,"E19.sketch_text.stroke-577")}),-1.0]])]});
            var Q38;
            Q38=makeQuery(id+"F0.imprint","IMPRINT",FACE,{"disambiguationData":[TD([[makeQuery(id+"F0.imprint","IMPRINT",EDGE,{"derivedFrom":sQuery(id+"F0.wireOp",EDGE,"E19.sketch_text.stroke-307")}),-1.0]])]});
            var Q39;
            Q39=makeQuery(id+"F0.imprint","IMPRINT",FACE,{"disambiguationData":[TD([[makeQuery(id+"F0.imprint","IMPRINT",EDGE,{"derivedFrom":sQuery(id+"F0.wireOp",EDGE,"E19.sketch_text.stroke-327")}),-1.0]])]});
            var Q40;
            Q40=makeQuery(id+"F0.imprint","IMPRINT",FACE,{"disambiguationData":[TD([[makeQuery(id+"F0.imprint","IMPRINT",EDGE,{"derivedFrom":sQuery(id+"F0.wireOp",EDGE,"E19.sketch_text.stroke-91")}),-1.0]])]});
            var Q41;
            Q41=makeQuery(id+"F0.imprint","IMPRINT",FACE,{"disambiguationData":[TD([[makeQuery(id+"F0.imprint","IMPRINT",EDGE,{"derivedFrom":sQuery(id+"F0.wireOp",EDGE,"E19.sketch_text.stroke-97")}),-1.0]])]});
            var Q42;
            Q42=makeQuery(id+"F0.imprint","IMPRINT",FACE,{"disambiguationData":[TD([[makeQuery(id+"F0.imprint","IMPRINT",EDGE,{"derivedFrom":sQuery(id+"F0.wireOp",EDGE,"E19.sketch_text.stroke-124")}),-1.0]])]});
            extrude(context, id + "F3", {"entities" : qUnion([Q0, Q1, Q2, Q3, Q4, Q5, Q6, Q7, Q8, Q9, Q10, Q11, Q12, Q13, Q14, Q15, Q16, Q17, Q18, Q19, Q20, Q21, Q22, Q23, Q24, Q25, Q26, Q27, Q28, Q29, Q30, Q31, Q32, Q33, Q34, Q35, Q36, Q37, Q38, Q39, Q40, Q41, Q42]), "depth" : 1 * mm, "hasSecondDirection" : true, "secondDirectionOppositeDirection" : true, "secondDirectionDepth" : -.2 * mm, "offsetDistance" : 25 * mm});
        }
    });
